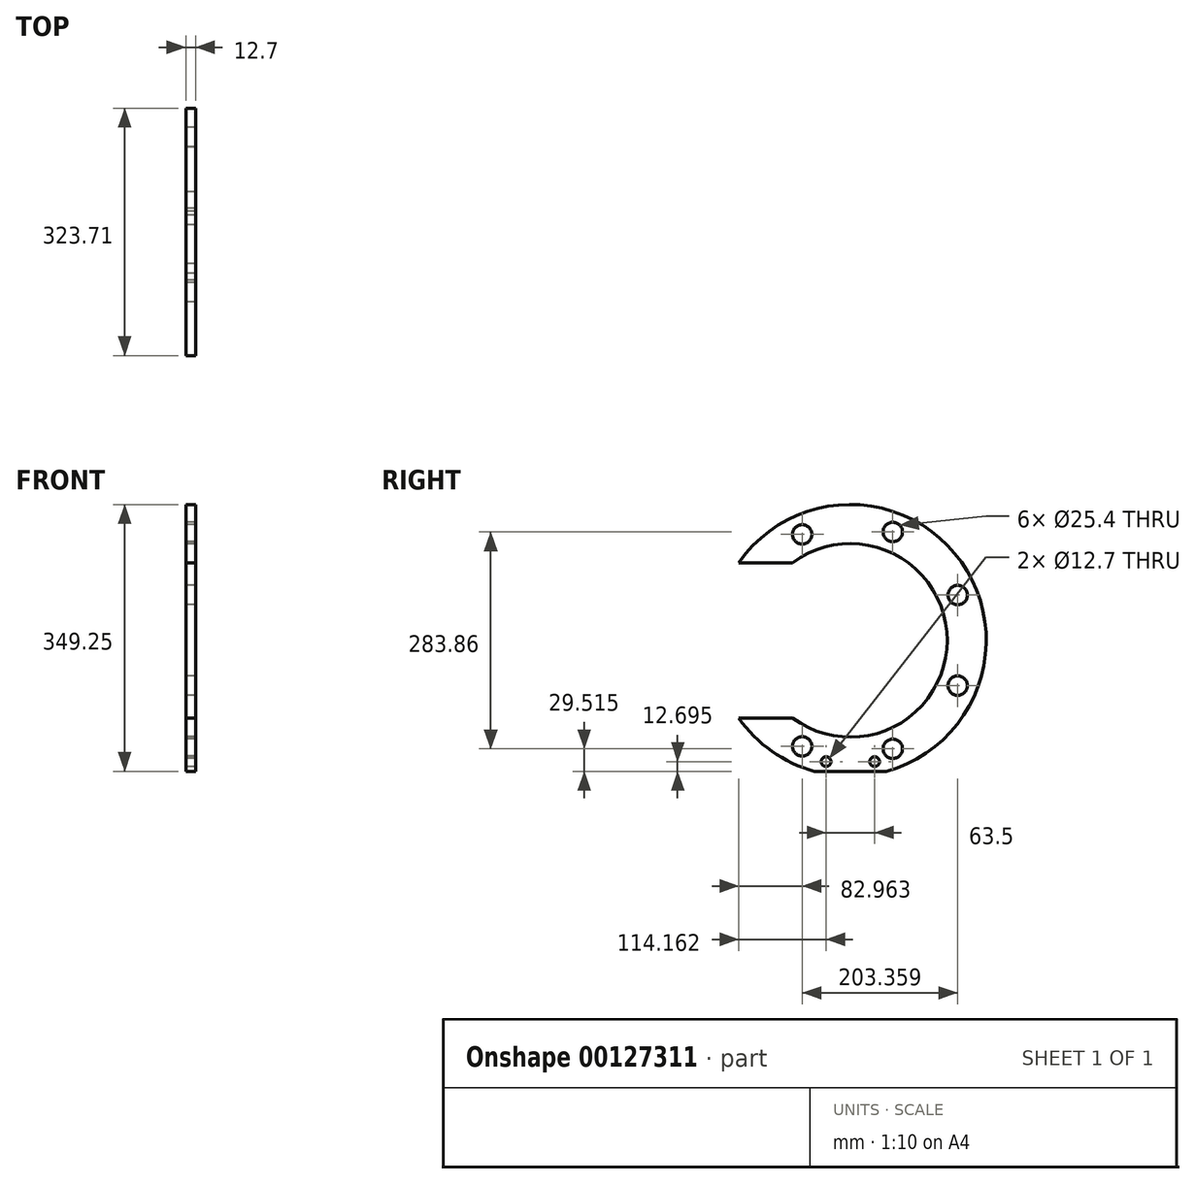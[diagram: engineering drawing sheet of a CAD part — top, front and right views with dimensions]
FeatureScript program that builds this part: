
annotation { "Feature Type Name" : "Feature", "Feature Type Description" : "" }
export const myFeature = defineFeature(function(context is Context, id is Id, definition is map)
    precondition{}
    {
        {
            var Q0;
            Q0=qCreatedBy(makeId("Right.planeOp"),FACE);
            var sketch = newSketch(context, id + "F0", { "sketchPlane" : qUnion([Q0])});
            skLineSegment(sketch, "E0.bottom", {"start": v(-294.65, 310.96) * mm, "end": v(60.95, 310.96) * mm, "construction": true});
            skLineSegment(sketch, "E0.top", {"start": v(-294.65, -44.64) * mm, "end": v(-223.45, -44.64) * mm, "construction": true});
            skLineSegment(sketch, "E0.left", {"start": v(-294.65, 310.96) * mm, "end": v(-294.65, -44.64) * mm, "construction": true});
            skLineSegment(sketch, "E0.right", {"start": v(60.95, 310.96) * mm, "end": v(60.95, -44.64) * mm, "construction": true});
            skArc(sketch, "E1", {"start": v(-262.76, 31.56) * mm, "mid": v(-219.48, -12.04) * mm, "end": v(-163.94, -38.3) * mm});
            skArc(sketch, "E2", {"start": v(-192.5, 31.56) * mm, "mid": v(9.82, 133.16) * mm, "end": v(-192.5, 234.76) * mm});
            skLineSegment(sketch, "E3.anchor2", {"start": v(-200.2, 5.8) * mm, "end": v(-200.3, 5.63) * mm, "construction": true});
            skLineSegment(sketch, "E4.top", {"start": v(-69.76, -38.3) * mm, "end": v(-163.94, -38.3) * mm});
            skLineSegment(sketch, "E5.trimOffspring", {"start": v(-28.08, -44.64) * mm, "end": v(60.95, -44.64) * mm, "construction": true});
            skArc(sketch, "E6.trimOffspring", {"start": v(-69.76, -38.3) * mm, "mid": v(28.34, 235.78) * mm, "end": v(-262.76, 234.76) * mm});
            skLineSegment(sketch, "E7.top", {"start": v(-262.76, 234.76) * mm, "end": v(-192.5, 234.76) * mm});
            skLineSegment(sketch, "E8.top", {"start": v(-262.76, 31.56) * mm, "end": v(-192.5, 31.56) * mm});
            skLineSegment(sketch, "E9.bottom", {"start": v(-192.5, 234.76) * mm, "end": v(-192.32, 234.76) * mm, "construction": true});
            skLineSegment(sketch, "E10", {"start": v(-116.85, 133.16) * mm, "end": v(-324.94, 133.16) * mm, "construction": true});
            skCircle(sketch, "E11", {"center": v(-227.63, 85.53) * mm, "radius": 38.1 * mm, "construction": true});
            skPoint(sketch, "E11.centerSnap0", {"position": v(-227.63, 31.56) * mm});
            skCircle(sketch, "E12", {"center": v(-227.63, 180.78) * mm, "radius": 38.1 * mm, "construction": true});
            skPoint(sketch, "E12.centerSnap0", {"position": v(-227.63, 234.76) * mm});
            skLineSegment(sketch, "E13.bottom", {"start": v(-192.5, 234.76) * mm, "end": v(-262.76, 234.76) * mm, "construction": true});
            skLineSegment(sketch, "E13.top", {"start": v(-192.5, 222.06) * mm, "end": v(-262.76, 222.06) * mm, "construction": true});
            skLineSegment(sketch, "E13.left", {"start": v(-192.5, 234.76) * mm, "end": v(-192.5, 222.06) * mm, "construction": true});
            skLineSegment(sketch, "E13.right", {"start": v(-262.76, 234.76) * mm, "end": v(-262.76, 222.06) * mm, "construction": true});
            skLineSegment(sketch, "E14.bottom", {"start": v(-192.5, 31.56) * mm, "end": v(-262.76, 31.56) * mm, "construction": true});
            skLineSegment(sketch, "E14.top", {"start": v(-192.5, 37.9) * mm, "end": v(-262.76, 37.9) * mm, "construction": true});
            skLineSegment(sketch, "E14.left", {"start": v(-192.5, 31.56) * mm, "end": v(-192.5, 37.9) * mm, "construction": true});
            skLineSegment(sketch, "E14.right", {"start": v(-262.76, 31.56) * mm, "end": v(-262.76, 37.9) * mm, "construction": true});
            skLineSegment(sketch, "E15.top", {"start": v(-192.5, 44.26) * mm, "end": v(-262.76, 44.26) * mm, "construction": true});
            skLineSegment(sketch, "E15.left", {"start": v(-192.5, 37.9) * mm, "end": v(-192.5, 44.26) * mm, "construction": true});
            skLineSegment(sketch, "E15.right", {"start": v(-262.76, 37.9) * mm, "end": v(-262.76, 44.26) * mm, "construction": true});
            skLineSegment(sketch, "E16", {"start": v(-192.5, 234.76) * mm, "end": v(-192.5, 336.03) * mm, "construction": true});
            skLineSegment(sketch, "E17", {"start": v(-192.5, 31.56) * mm, "end": v(-192.5, -66.78) * mm, "construction": true});
            skCircle(sketch, "E18", {"center": v(-116.85, 133.16) * mm, "radius": 152.4 * mm, "construction": true});
            skCircle(sketch, "E19", {"center": v(-179.8, 271.95) * mm, "radius": 12.7 * mm});
            skCircle(sketch, "E20.1.0", {"center": v(-61.34, 275.08) * mm, "radius": 12.7 * mm});
            skCircle(sketch, "E20.2.0", {"center": v(23.56, 192.4) * mm, "radius": 12.7 * mm});
            skCircle(sketch, "E20.3.0", {"center": v(23.56, 73.9) * mm, "radius": 12.7 * mm});
            skCircle(sketch, "E20.4.0", {"center": v(-61.34, -8.77) * mm, "radius": 12.7 * mm});
            skCircle(sketch, "E20.5.0", {"center": v(-179.8, -5.64) * mm, "radius": 12.7 * mm});
            skLineSegment(sketch, "E20.anchor1", {"start": v(-116.85, 133.16) * mm, "end": v(-179.8, 271.95) * mm, "construction": true});
            skLineSegment(sketch, "E20.anchor2", {"start": v(-116.85, 133.16) * mm, "end": v(-179.8, -5.64) * mm, "construction": true});
            skLineSegment(sketch, "E21", {"start": v(-116.85, -38.3) * mm, "end": v(-116.85, -25.6) * mm, "construction": true});
            skLineSegment(sketch, "E22", {"start": v(-85.1, -25.6) * mm, "end": v(-148.6, -25.6) * mm, "construction": true});
            skCircle(sketch, "E23", {"center": v(-85.1, -25.6) * mm, "radius": 6.35 * mm});
            skCircle(sketch, "E24", {"center": v(-148.6, -25.6) * mm, "radius": 6.35 * mm});
            skSolve(sketch);
        }
        {
            var Q0;
            {var subQ0=sQuery(id+"F0.wireOp",EDGE,"E1");Q0=makeQuery(id+"F0.imprint","IMPRINT",FACE,{"disambiguationData":[TD([[makeQuery(id+"F0.imprint","IMPRINT",EDGE,{"derivedFrom":subQ0}),1.0]])]});}
            extrude(context, id + "F1", {"entities" : qUnion([Q0]), "depth" : 12.7 * mm});
        }
    });
